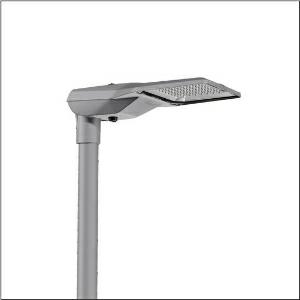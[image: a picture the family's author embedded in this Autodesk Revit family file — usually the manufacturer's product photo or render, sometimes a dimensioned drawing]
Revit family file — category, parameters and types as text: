
# Revit family: streetlight_sl_21_iq_midi___st0_5a_5xe3b31y08nb_abd3
name_source: partatom
category: Lighting Fixtures
units: mm (PartAtom-declared; Revit-internal decimal feet)

## family parameters
Cut with Voids When Loaded = No
Host = Face
Light Source = No
Part Type = Normal
Room Calculation Point = No
Round Connector Dimension = Use Diameter
Shared = No

## types (1)
- --- (1 x LED, 21550 lm, 136.6 W, 3000K)
    Apparent Load = 137 VA
    CIE Flux Codes = 43 76 97 100 100
    Color Rendering = 70
    Color Temperature = 3000K
    Default Elevation = 1800 mm
    Description = Streetlight SL 21 iQ midi, mast luminaire, primary light control with lens, of PMMA, primary optical cover: cover, of toughened safety glass, transparent, light distribution: ST0.5a, light emission: direct distribution, primary light characteristic: asymmetric, installation type: post-top, side-entry, LED, High Power LED, rated luminous flux: 21.550lm, luminous efficacy: 158lm/W, light colour: 730, colour temperature: 3000K, control gear: iQ-Street Remote, D4i with power reduction, control: pre-setting: logarithmic dimming characteristic, Street-Remote, Auto-Match, Temp-Guard, Lumen-Switch, Night-Set, Smart-Wire, Light-Fading, Desk-Remote (wireless, voltage-free reading and setting of iQ features in the workshop via application-optimized NFC function/RFID function), optimised constant luminous flux control (CLO 2.0), mains connection: 230..240V, AC, 50/60Hz, start of lifetime: 137W, end of service life: 144W, reduction: 61W, luminaire housing, of diecast aluminium, powder-coated, Siteco® metallic grey (DB 702S), corrosivity category C5 mid according to DIN EN ISO 12944, please order mast flange separately, inclination adjustable: 0°, 5°, 10°, 15°, sealing non-destructively replaceable, multi-level sealing system, length: 644mm, width: 335mm, height: 110mm, mast flange for spigot size: 42mm (side-entry): 5XC10008XM4, 60/48mm (side-entry/post-top): 5XC10108XM2, 76/60mm (side-entry/post-top): 5XC10108XM1, mounting height: 4..8m, Smart Interface below and above, protection rating (complete): IP66, insulation class (complete): insulation class II (safety insulation), certification: CE, ENEC, ENEC+, VDE, impact resistance: IK10, permissible operating ambient temperature for outdoor applications: -40..+50°C, standard-compliant lighting for roads and squares, packaging unit: 1 piece

Light Distribution: ST0.5a
    Height = 111 mm
    Lamp = 1 x LED
    Lamp Light Flux = 21550 lm
    Lamp Power = 136.6 W
    Lamp count = 1
    Length = 644 mm
    Luminous efficacy = 158 lm/W
    Manufacturer = Siteco
    ModVariant = No
    Model = 5XE3B31Y08NB
    Number of Poles = 1
    OnlyDefault = Yes
    Power Factor = 1
    Product Name = Streetlight SL 21 iQ midi | ST0.5a
    Product group = mast luminaire | pylon top
    ProductGroupID = 6100
    Protection Class = Protection class II
    Protection Degree = IP 66
    RLX_Detail_Level = 1
    RLX_Emergency_Light_Flux = 0 lm
    RLX_Emergency_Type = 0
    RLX_Emergency_Type_DB = No
    RlxData = <blob elided: 102329 chars, md5=9794a9c4>
    Socket = socket
    Standby Power = 0 W
    System Light Flux = 21550 lm
    System Power = 137 W
    Type Comments = factory setting: luminous flux: 100 % | dim-lin: 254 | 733 mA
    Type Image = l_1004304.jpg
    URL = http://relux.com
    VarID = @adj_137275
    Voltage = 0 V
    Weight = 0.00 kg
    Width = 336 mm

## geometry (parser evidence)
native form markers: Blend x4, Sweep x11
no freeform markers — native parametric forms only
